# Revit family: Shower-Shower_Door-STERLING-Finesse-5485_1
name_source: partatom
category: Specialty Equipment
revit_build: Autodesk Revit 2015 (Build: 20140606_1530(x64)
units: mm (PartAtom-declared; Revit-internal decimal feet)

## types (1)
- N-Nickel with Lake Mist Glass Pattern
    ADA Compliant = No
    Assembly Code = C1030200
    Date Modified = 6/10/2019
    Default Elevation = 0"
    Description = Frameless Sliding Shower Door
    Finish = Sterling-Metal-N-Nickel
    Glass Material = Sterling-Glass-G69-Lake_Mist_Glass_Pattern
    Height = 72"
    Length = 2 1/2"
    Manufacturer = STERLING Co.
    MasterFormat 1995 = 10820
    MasterFormat 2004 = 10.28.13
    Material = Nickel frame finish
    Model = 5485-48N-G69
    Product Documentation Link = https://resources.kohler.com
    Product Name = Finesse
    Product Page URL = http://www.sterlingplumbing.com
    URL = https://www.sterlingplumbing.com
    WaterSense Certified = No

## geometry (parser evidence)
native form markers: Sweep x5
no freeform markers — native parametric forms only
